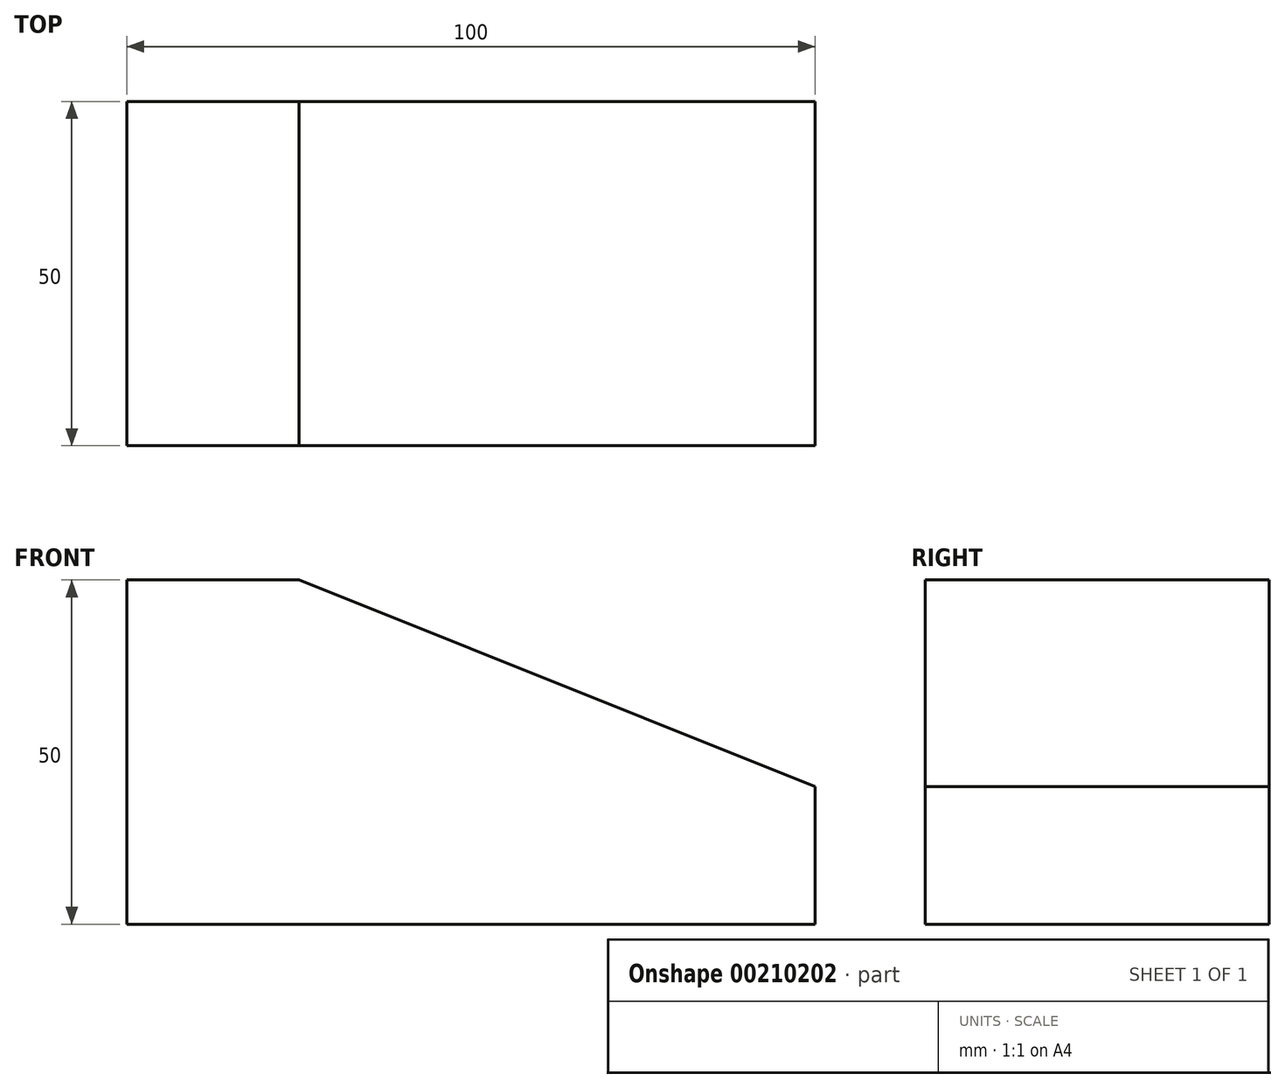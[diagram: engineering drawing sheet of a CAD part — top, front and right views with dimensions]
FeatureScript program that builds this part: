
annotation { "Feature Type Name" : "Feature", "Feature Type Description" : "" }
export const myFeature = defineFeature(function(context is Context, id is Id, definition is map)
    precondition{}
    {
        {
            var Q0;
            Q0=qCreatedBy(makeId("Front.planeOp"),FACE);
            var sketch = newSketch(context, id + "F0", { "sketchPlane" : qUnion([Q0])});
            skLineSegment(sketch, "E0", {"start": v(0, 0) * mm, "end": v(100, 0) * mm});
            skLineSegment(sketch, "E1", {"start": v(100, 0) * mm, "end": v(100, 20) * mm});
            skLineSegment(sketch, "E2", {"start": v(100, 20) * mm, "end": v(25, 50) * mm});
            skLineSegment(sketch, "E3", {"start": v(25, 50) * mm, "end": v(0, 50) * mm});
            skLineSegment(sketch, "E4", {"start": v(0, 50) * mm, "end": v(0, 0) * mm});
            skSolve(sketch);
        }
        {
            var Q0;
            Q0 = qSketchRegion(id + "F0", true);
            extrude(context, id + "F1", {"entities" : qUnion([Q0]), "depth" : 50 * mm});
        }
    });
